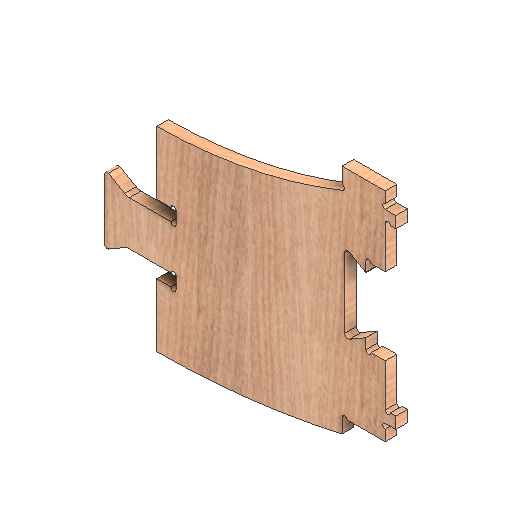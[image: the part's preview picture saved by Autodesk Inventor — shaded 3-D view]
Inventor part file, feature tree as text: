
AUTODESK INVENTOR PART (.ipt)
format: ipt  version: 2021 (Build 250183000, 183)  size: 371,200 bytes
history: native  units: mm
features: other x2, extrude x1
ambient origin geometry x8: Origin, YZ Plane, XZ Plane, XY Plane, X Axis, Y Axis, Z Axis, Center Point
bodies: Solid1 (feature_tree)
feature tree (3):
  other  "CONTOURS"
  other  "LETTERS"
  extrude  "Extrusion1"  Depth=18.0mm TaperAngle=0.0deg
